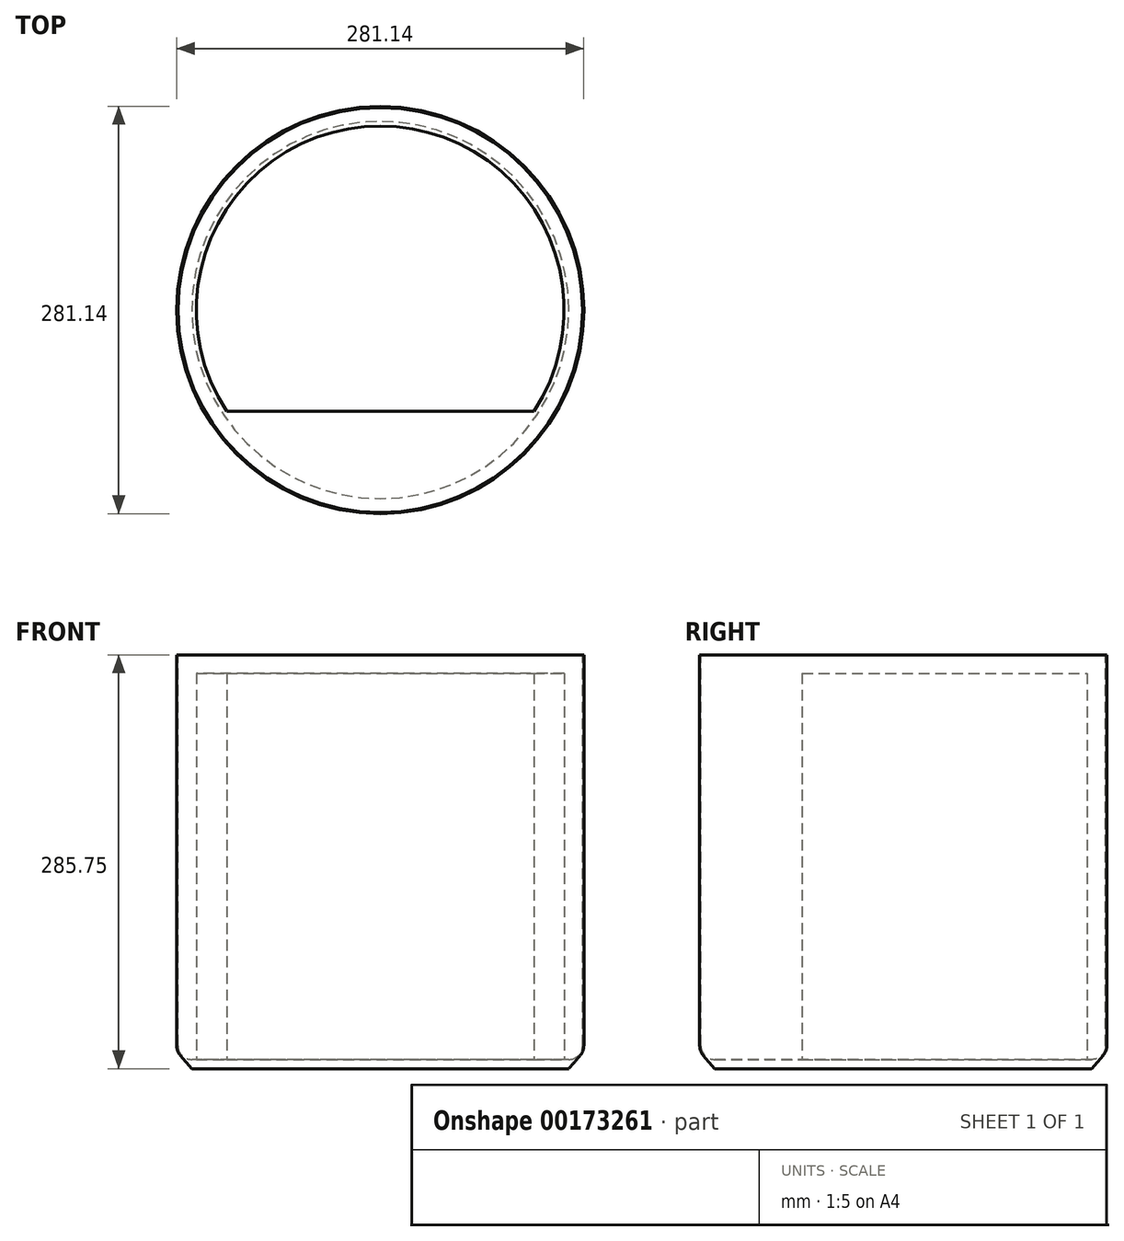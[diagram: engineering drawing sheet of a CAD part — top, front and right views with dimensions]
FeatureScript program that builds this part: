
annotation { "Feature Type Name" : "Feature", "Feature Type Description" : "" }
export const myFeature = defineFeature(function(context is Context, id is Id, definition is map)
    precondition{}
    {
        {
            var Q0;
            Q0=qCreatedBy(makeId("Top.planeOp"),FACE);
            var sketch = newSketch(context, id + "F0", { "sketchPlane" : qUnion([Q0])});
            skLineSegment(sketch, "E0", {"start": v(-106.07, -69.85) * mm, "end": v(106.07, -69.85) * mm});
            skArc(sketch, "E1", {"start": v(106.07, -69.85) * mm, "mid": v(0, 127) * mm, "end": v(-106.07, -69.85) * mm});
            skSolve(sketch);
        }
        {
            var Q0;
            Q0=makeQuery(id+"F0.imprint","IMPRINT",FACE,{"disambiguationData":[TD([[makeQuery(id+"F0.imprint","IMPRINT",EDGE,{"derivedFrom":sQuery(id+"F0.wireOp",EDGE,"E0")}),1.0]])]});
            extrude(context, id + "F1", {"entities" : qUnion([Q0]), "depth" : 266.7 * mm});
        }
        {
            var Q0;
            Q0=qCreatedBy(makeId("Front.planeOp"),FACE);
            var sketch = newSketch(context, id + "F2", { "sketchPlane" : qUnion([Q0])});
            skLineSegment(sketch, "E2", {"start": v(0, 0) * mm, "end": v(-130.18, 0) * mm});
            skLineSegment(sketch, "E3", {"start": v(-139.7, 9.52) * mm, "end": v(-139.7, 279.4) * mm});
            skPoint(sketch, "E4.visualSharp", {"position": v(-139.7, 0) * mm});
            skArc(sketch, "E4.filletArc", {"start": v(-139.7, 9.52) * mm, "mid": v(-136.91, 2.79) * mm, "end": v(-130.18, 0) * mm});
            skLineSegment(sketch, "E5.0", {"start": v(-140.57, 9.52) * mm, "end": v(-140.57, 279.4) * mm});
            skArc(sketch, "E5.1", {"start": v(-140.57, 9.52) * mm, "mid": v(-137.53, 2.17) * mm, "end": v(-130.18, -0.87) * mm});
            skLineSegment(sketch, "E5.2", {"start": v(0, -0.87) * mm, "end": v(-130.18, -0.87) * mm});
            skLineSegment(sketch, "E6", {"start": v(-140.57, 279.4) * mm, "end": v(-139.7, 279.4) * mm});
            skLineSegment(sketch, "E7", {"start": v(0, 0) * mm, "end": v(0, -6.35) * mm});
            skLineSegment(sketch, "E8", {"start": v(0, -6.35) * mm, "end": v(-130.18, -6.35) * mm});
            skLineSegment(sketch, "E9", {"start": v(-130.18, -6.35) * mm, "end": v(-138.03, 2.71) * mm});
            skLineSegment(sketch, "E10", {"start": v(-130.18, -0.87) * mm, "end": v(-133.35, -0.87) * mm, "construction": true});
            skLineSegment(sketch, "E11", {"start": v(-133.35, -0.87) * mm, "end": v(-133.35, 0.54) * mm, "construction": true});
            skSolve(sketch);
        }
        {
            var Q0;
            {var subQ2=sQuery(id+"F2.wireOp",EDGE,"E2");Q0=makeQuery(id+"F2.imprint","IMPRINT",FACE,{"disambiguationData":[TD([[makeQuery(id+"F2.imprint","IMPRINT",EDGE,{"derivedFrom":subQ2}),1.0]])]});}
            var Q1;
            {var subQ2=sQuery(id+"F2.wireOp",EDGE,"E5.2");Q1=makeQuery(id+"F2.imprint","IMPRINT",FACE,{"disambiguationData":[TD([[makeQuery(id+"F2.imprint","IMPRINT",EDGE,{"derivedFrom":subQ2}),1.0]])]});}
            var Q2;
            Q2=sQuery(id+"F2.wireOp",EDGE,"E7");
            revolve(context, id + "F3", {"entities" : qUnion([Q0, Q1]), "axis" : qUnion([Q2]), "revolveType" : RevolveType.FULL});
        }
    });
